# Revit family: PT
name_source: partatom
category: Lighting Fixtures
revit_build: Autodesk Revit MEP 2012 (Build: 20110309_2315(x64)
units: mm (PartAtom-declared; Revit-internal decimal feet)

## types (1)
- PT
    Apparent Load = 0 VA
    Back Plate = Hubbell - Antique Bronze
    Color Filter = 16777215
    Default Elevation = 48.00"
    Description = One-light Bath
    Dimming Lamp Color Temperature Shift = <None>
    Glass = Hubbell - Glass
    Lamp = Bulb - Uses Candelabra Base
    Load Classification = Lighting
    Manufacturer = Progresslighting
    Manufacturer Fax Number = (864)-678-1065
    Model = P300035-020
    Mounting = Wall Mounted
    Photometric Web File = generic
    Product Documentation Link = https://media.progresslighting.com
    Product Page URL = https://progresslighting.com
    Tilt Angle = 0.00°
    URL = https://progresslighting.com
    Voltage = 0 V
    Wattage = 60 VA
    Wattage Comments = 60

## geometry (parser evidence)
native form markers: Blend x2, Sweep x1
no freeform markers — native parametric forms only
